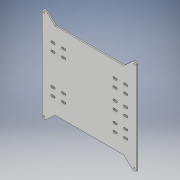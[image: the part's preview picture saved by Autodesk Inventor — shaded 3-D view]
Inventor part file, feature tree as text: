
AUTODESK INVENTOR PART (.ipt)
format: ipt  version: 2017 (Build 210142000, 142)  size: 315,392 bytes
history: native  units: in
note: dims shown in document units (in); Inventor stores cm internally (conversion verified against a paired STEP export)
features: extrude x4, sketch x4, projected_geometry x2, fillet x1
ambient origin geometry x8: Origin, YZ Plane, XZ Plane, XY Plane, X Axis, Y Axis, Z Axis, Center Point
bodies: Solid1 (feature_tree)
feature tree (11):
  extrude  "Extrusion1"  Depth=8.5827in
  fillet  "Fillet1"  Radius=0.1181in
  extrude  "Extrusion2"  Depth=0.7874in
  extrude  "Extrusion3"  Depth=1.1811in
  extrude  "Extrusion4"  Depth=0.8657in
  sketch  "Sketch1"  dims[d0=8.5827in d1=8.5827in d2=0.1181in d3=0.0in]
  sketch  "Sketch2"  dims[d4=0.125in d5=0.7874in]
  projected_geometry  "Projected Loop1"
  sketch  "Sketch3"  dims[d6=1.1811in d7=1.1811in]
  projected_geometry  "Projected Loop2"
  sketch  "Sketch4"  dims[d8=0.7874in d9=0.1969in d10=0.1969in d11=0.1181in d12=0.0in d13=0.387in d14=0.177in d15=0.8in d16=1.31in d17=0.387in d18=0.177in d19=0.8in d20=0.5315in d21=1.31in d22=0.177in d23=0.387in d24=0.575in d25=0.5315in d26=0.177in d27=0.387in d28=0.575in d29=0.575in d30=0.387in d31=0.387in d32=0.177in d33=0.177in d34=0.177in d35=0.177in d36=0.387in d37=0.387in d38=0.5315in d39=0.8in d40=0.8657in d41=0.8657in d42=1.0in d43=0.0in d44=0.137in d45=0.13in d46=0.135in d47=0.137in d48=0.135in d49=0.13in d50=0.137in d51=0.135in d52=0.13in d53=0.137in d54=0.135in d55=0.13in d56=1.0in d57=0.0in]
